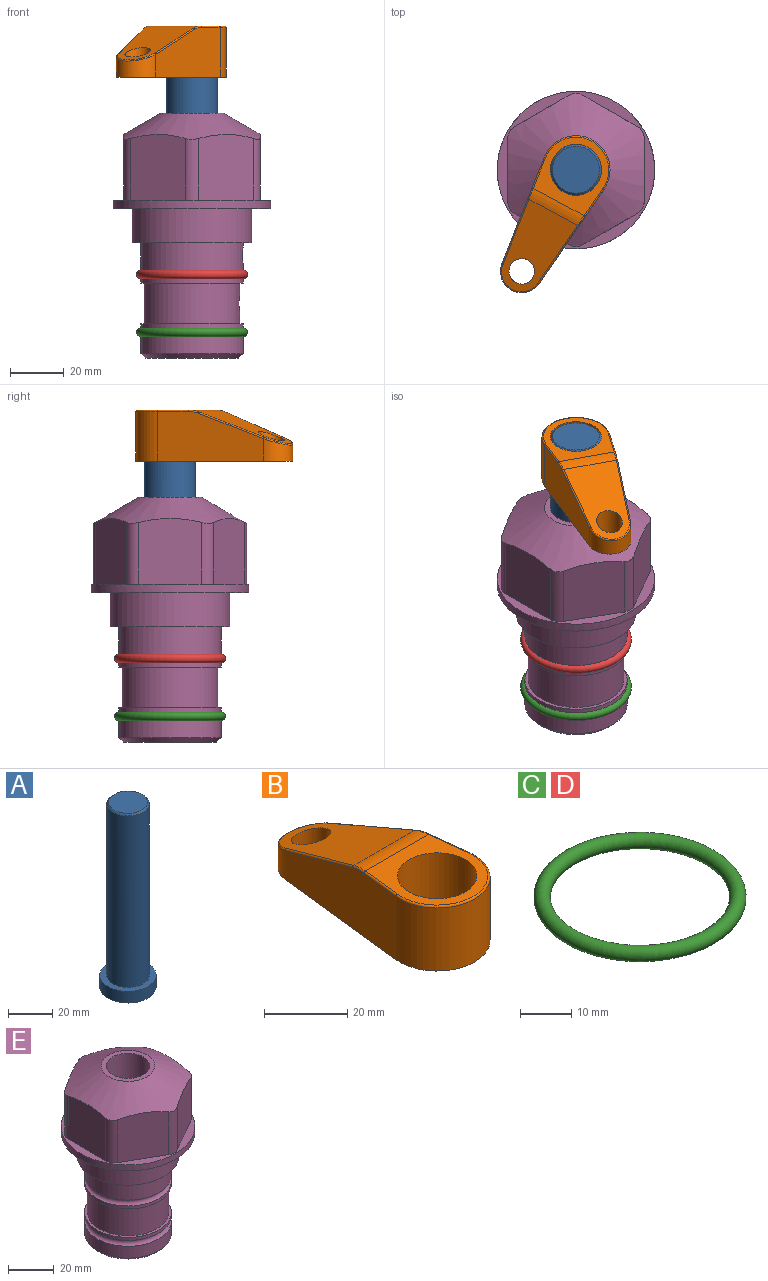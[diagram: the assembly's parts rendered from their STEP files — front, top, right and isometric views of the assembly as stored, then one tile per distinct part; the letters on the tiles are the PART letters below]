
ASSEMBLY  parts=5 mates=3
PART A: 6 faces, bbox 25.4x25.4x101.6 mm
  f0: plane 17.46x17.46mm, normal (0,0,1), area 239.5mm2, adj f5
  f1: plane 25.4x25.4mm, normal (0,0,-1), area 506.7mm2, adj f2
  f2: cylinder r=12.7mm len=25.4mm, axis (0,0,1), area 506.7mm2, adj f1,f3
  f3: plane 25.4x25.4mm, normal (0,0,1), area 221.7mm2, adj f2,f4
  f4: cylinder r=9.53mm len=94.46mm, axis (0,0,1), area 5653mm2, adj f3,f5
  f5: cone r=8.73mm half-angle=45deg, axis (0,0,-1), area 64.4mm2, adj f0,f4
PART B: 44 faces, bbox 27.5x64.5x19.1 mm
  f0: plane 2.3x0.95mm, normal (0,0,-1), area 1mm2, adj f25,f30,f34
  f1: plane 63.5x25.4mm, normal (0,0,-1), area 561.7mm2, adj f2,f3,f4,f5,f6,f7,f19,f20
  f2: cylinder r=12.7mm len=25.4mm, axis (0,0,-1), area 792.2mm2, adj f1,f3,f5,f13
  f3: plane 42.33x18.54mm, normal (0.99,0.11,0), area 647mm2, adj f1,f2,f4,f11,f12,f14
  f4: cylinder r=7.94mm len=15.78mm, axis (0,0,-1), area 158.6mm2, adj f1,f3,f5,f16
  f5: plane 42.33x18.54mm, normal (-0.99,0.11,0), area 647mm2, adj f1,f2,f4,f15,f17,f18
  f6: cylinder r=9.53mm len=19.05mm, axis (0,0,-1), area 1140.1mm2, adj f1,f8
  f7: cylinder r=4.76mm len=10.98mm, axis (0,0,-1), area 276.1mm2, adj f1,f9
  f8: plane 25.83x24.38mm, normal (0,0,1), area 262.2mm2, adj f6,f10,f11,f13,f15
  f9: plane 32.49x20.55mm, normal (0,0.34,0.94), area 489.9mm2, adj f7,f10,f14,f16,f18
  f10: cylinder r=12.7mm len=21.49mm, axis (-1,0,0), area 93.2mm2, adj f8,f9,f12,f17
  f11: cylinder r=0.51mm len=12.34mm, axis (0.11,-0.99,0), area 9.9mm2, adj f3,f8,f12,f13
  f12: bspline ~7.62x1.64mm, area 3.5mm2, adj f3,f10,f11,f14
  f13: torus R=12.19mm, axis (0,0,1), area 33.6mm2, adj f2,f8,f11,f15
  f14: cylinder r=0.51mm len=26.01mm, axis (0.1,-0.93,0.34), area 21.6mm2, adj f3,f9,f12,f16
  f15: cylinder r=0.51mm len=12.34mm, axis (0.11,0.99,0), area 9.9mm2, adj f5,f8,f13,f17
  f16: bspline ~15.78x7.05mm, area 15.7mm2, adj f4,f9,f14,f18
  f17: bspline ~7.62x1.64mm, area 3.5mm2, adj f5,f10,f15,f18
  f18: cylinder r=0.51mm len=26.01mm, axis (0.1,0.93,-0.34), area 21.6mm2, adj f5,f9,f16,f17
  f19: plane 21.6x14.29mm, normal (-0.99,-0.11,0), area 242.6mm2, adj f1,f26,f28,f34,f36,f38
  f20: plane 21.6x14.29mm, normal (0.99,-0.11,0), area 242.6mm2, adj f1,f27,f29,f37,f39,f41
  f21: cylinder r=12.7mm len=14.29mm, axis (0,0,-1), area 173.2mm2, adj f1,f26,f27,f30,f31,f33
  f22: cylinder r=7.94mm len=7.63mm, axis (0,0,-1), area 53.8mm2, adj f1,f28,f29,f42
  f23: plane 2.3x0.95mm, normal (0,0,-1), area 1mm2, adj f25,f33,f37
  f24: plane 17.94x12.32mm, normal (0,-0.34,-0.94), area 191.2mm2, adj f25,f38,f41,f42
  f25: cylinder r=9.53mm len=12.93mm, axis (-1,0,0), area 37.5mm2, adj f0,f23,f24,f31,f36,f39
  f26: cylinder r=1.59mm len=14.29mm, axis (0,0,-1), area 49mm2, adj f1,f19,f21,f32
  f27: cylinder r=1.59mm len=14.29mm, axis (0,0,-1), area 49mm2, adj f1,f20,f21,f35
  f28: cylinder r=1.59mm len=7.28mm, axis (0,0,-1), area 22.1mm2, adj f1,f19,f22,f40
  f29: cylinder r=1.59mm len=7.28mm, axis (0,0,-1), area 22.1mm2, adj f1,f20,f22,f43
  f30: torus R=14.29mm, axis (0,0,1), area 5.8mm2, adj f0,f21,f31,f32
  f31: bspline ~11.06x2.73mm, area 20.8mm2, adj f21,f25,f30,f33
  f32: sphere r=1.59mm, area 5.4mm2, adj f26,f30,f34
  f33: torus R=14.29mm, axis (0,0,1), area 5.8mm2, adj f21,f23,f31,f35
  f34: cylinder r=1.59mm len=1.68mm, axis (-0.11,0.99,0), area 2.4mm2, adj f0,f19,f32,f36
  f35: sphere r=1.59mm, area 5.4mm2, adj f27,f33,f37
  f36: bspline ~5.82x2.33mm, area 7.7mm2, adj f19,f25,f34,f38
  f37: cylinder r=1.59mm len=1.68mm, axis (0.11,0.99,0), area 2.4mm2, adj f20,f23,f35,f39
  f38: cylinder r=1.59mm len=18.33mm, axis (0.1,-0.93,0.34), area 46.7mm2, adj f19,f24,f36,f40
  f39: bspline ~5.82x2.33mm, area 7.7mm2, adj f20,f25,f37,f41
  f40: sphere r=1.59mm, area 3.6mm2, adj f28,f38,f42
  f41: cylinder r=1.59mm len=18.33mm, axis (0.1,0.93,-0.34), area 46.7mm2, adj f20,f24,f39,f43
  f42: bspline ~8.31x1.84mm, area 15.3mm2, adj f22,f24,f40,f43
  f43: sphere r=1.59mm, area 3.6mm2, adj f29,f41,f42
PART C: 1 faces, bbox 44.7x44.7x3.2 mm
  f0: torus R=19.05mm, axis (0,0,1), area 1193.9mm2
PART D: same geometry as C
PART E: 36 faces, bbox 58.7x58.7x91.2 mm
  f0: cylinder r=17.78mm len=35.56mm, axis (0,0,1), area 1670.8mm2, adj f23,f24,f31
  f1: cylinder r=19.05mm len=38.1mm, axis (0,0,1), area 1191.9mm2, adj f26,f27,f30
  f2: plane 58.66x58.66mm, normal (0,0,-1), area 1150.6mm2, adj f3,f28
  f3: cylinder r=29.33mm len=58.66mm, axis (0,0,-1), area 585.1mm2, adj f2,f4
  f4: plane 58.66x58.66mm, normal (0,0,1), area 475.9mm2, adj f3,f5,f6,f7,f8,f9,f10,f11
  f5: plane 24.5x20.32mm, normal (-0.5,0.87,0), area 562.8mm2, adj f4,f15,f16,f17
  f6: plane 24.5x20.32mm, normal (0.5,0.87,0), area 562.8mm2, adj f4,f14,f15,f17
  f7: plane 24.5x23.48mm, normal (1,0,0), area 562.8mm2, adj f4,f13,f14,f17
  f8: plane 24.5x20.32mm, normal (0.5,-0.87,0), area 562.8mm2, adj f4,f12,f13,f17
  f9: plane 24.5x20.32mm, normal (-0.5,-0.87,0), area 562.8mm2, adj f4,f11,f12,f17
  f10: plane 24.5x23.48mm, normal (-1,0,0), area 562.8mm2, adj f4,f11,f16,f17
  f11: cylinder r=5.08mm len=23.01mm, axis (0,0,-1), area 121.2mm2, adj f4,f9,f10,f17
  f12: cylinder r=5.08mm len=23.01mm, axis (0,0,-1), area 121.2mm2, adj f4,f8,f9,f17
  f13: cylinder r=5.08mm len=23.01mm, axis (0,0,-1), area 121.2mm2, adj f4,f7,f8,f17
  f14: cylinder r=5.08mm len=23.01mm, axis (0,0,-1), area 121.2mm2, adj f4,f6,f7,f17
  f15: cylinder r=5.08mm len=23.01mm, axis (0,0,-1), area 121.2mm2, adj f4,f5,f6,f17
  f16: cylinder r=5.08mm len=23.01mm, axis (0,0,-1), area 121.2mm2, adj f4,f5,f10,f17
  f17: cone r=11.73mm half-angle=60deg, axis (0,0,-1), area 2071.8mm2, adj f5,f6,f7,f8,f9,f10,f11,f12
  f18: plane 23.46x23.46mm, normal (0,0,1), area 147.4mm2, adj f17,f35
  f19: plane 34.93x34.93mm, normal (0,0,-1), area 958mm2, adj f29
  f20: cylinder r=19.05mm len=38.1mm, axis (0,0,1), area 760.1mm2, adj f21,f29
  f21: torus R=19.05mm, axis (0,0,1), area 565.3mm2, adj f20,f22
  f22: cylinder r=19.05mm len=38.1mm, axis (0,0,1), area 190mm2, adj f21,f23
  f23: plane 38.1x38.1mm, normal (0,0,1), area 146.9mm2, adj f0,f22
  f24: plane 38.1x38.1mm, normal (0,0,-1), area 146.9mm2, adj f0,f25
  f25: cylinder r=19.05mm len=38.1mm, axis (0,0,1), area 190mm2, adj f24,f26
  f26: torus R=19.05mm, axis (0,0,1), area 565.3mm2, adj f1,f25
  f27: plane 44.45x44.45mm, normal (0,0,-1), area 411.7mm2, adj f1,f28
  f28: cylinder r=22.23mm len=44.45mm, axis (0,0,1), area 1773.5mm2, adj f2,f27
  f29: cone r=19.05mm half-angle=45deg, axis (0,0,1), area 257.5mm2, adj f19,f20
  f30: cylinder r=3.17mm len=6.75mm, axis (-1,0,0), area 128mm2, adj f1,f33
  f31: cylinder r=3.17mm len=6.35mm, axis (-1,0,0), area 102.5mm2, adj f0,f33
  f32: plane 25.4x25.4mm, normal (0,0,1), area 506.7mm2, adj f33
  f33: cylinder r=12.7mm len=66.42mm, axis (0,0,-1), area 5236.2mm2, adj f30,f31,f32,f34
  f34: cone r=9.53mm half-angle=30deg, axis (0,0,-1), area 443.4mm2, adj f33,f35
  f35: cylinder r=9.53mm len=19.05mm, axis (0,0,-1), area 849mm2, adj f18,f34
PLACE A rot(axis=(0,0,-1),118.1deg) t=(0,0,-5.59)mm
PLACE B rot(axis=(0,0,1),151.9deg) t=(0,0,49.02)mm
PLACE C t=(0,0,-21.59)mm
PLACE D at identity
PLACE E at identity fixed
MATE fastened C.f0 <-> E.f0  axis (0,0,1) through (0,0,-46.1)mm
MATE cylindrical A.f2 <-> E.f0  axis (0,0,1) through (0,0,20.05)mm
MATE fastened B.f2 <-> A.f2  axis (0,0,1) through (0,0,68.07)mm
